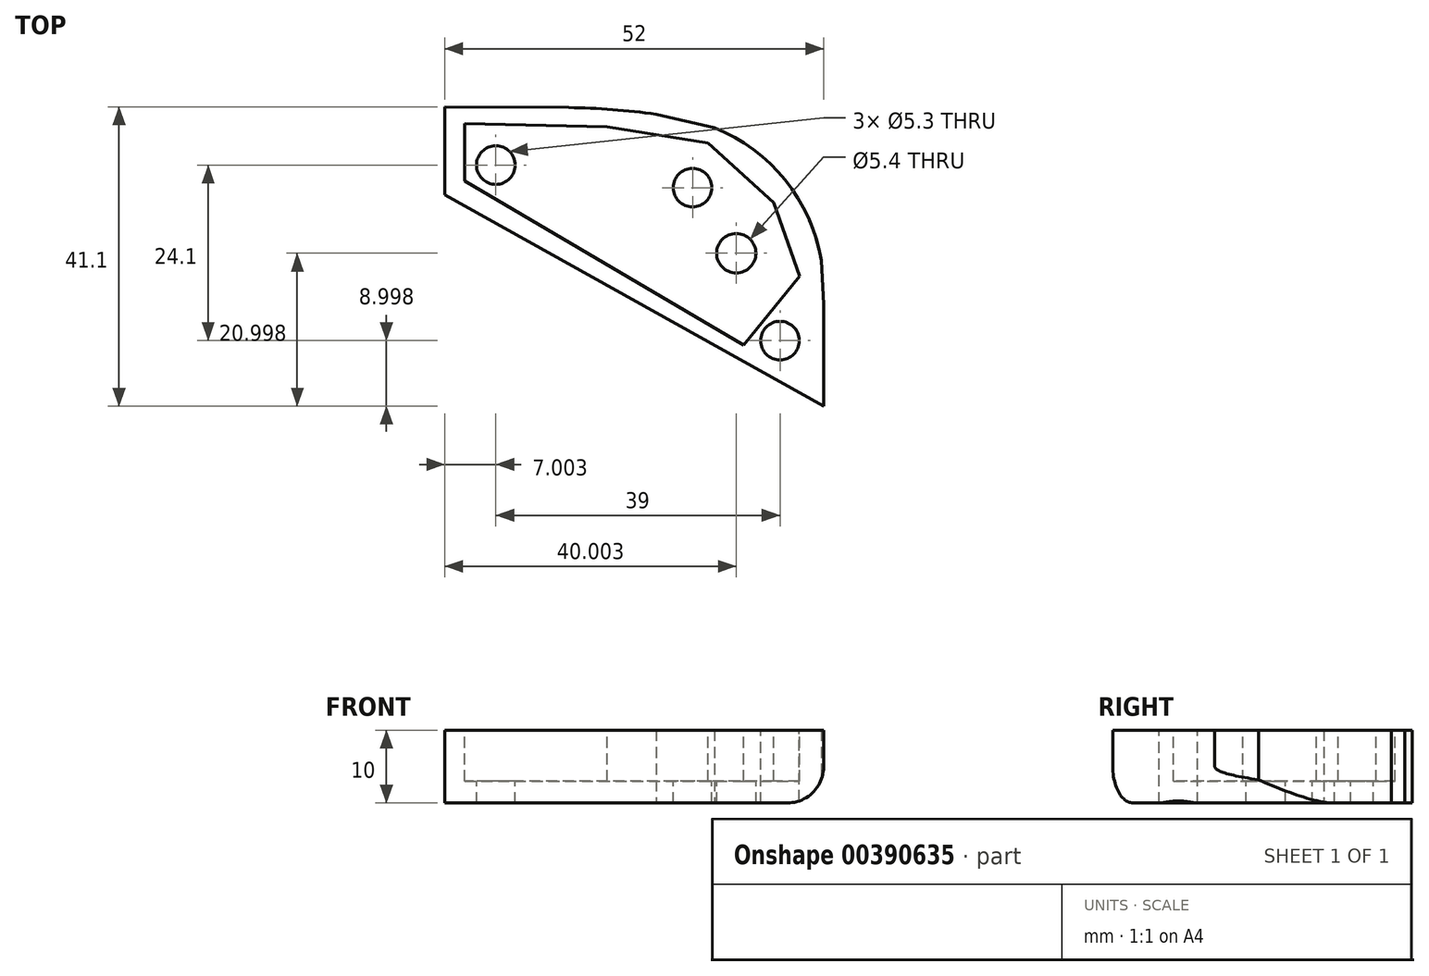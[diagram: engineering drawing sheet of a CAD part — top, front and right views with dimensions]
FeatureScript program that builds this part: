
annotation { "Feature Type Name" : "Feature", "Feature Type Description" : "" }
export const myFeature = defineFeature(function(context is Context, id is Id, definition is map)
    precondition{}
    {
        {
            var Q0;
            Q0=qCreatedBy(makeId("Top.planeOp"),FACE);
            var sketch = newSketch(context, id + "F0", { "sketchPlane" : qUnion([Q0])});
            skLineSegment(sketch, "E0", {"start": v(-50.84, -9.15) * mm, "end": v(-50.84, -21.25) * mm});
            skLineSegment(sketch, "E1", {"start": v(1.16, -50.25) * mm, "end": v(-50.84, -21.25) * mm});
            skLineSegment(sketch, "E2", {"start": v(1.16, -50.25) * mm, "end": v(1.16, -36.25) * mm});
            skArc(sketch, "E3", {"start": v(-13.84, -12) * mm, "mid": v(-4.13, -19.22) * mm, "end": v(0.83, -30.25) * mm});
            skLineSegment(sketch, "E4", {"start": v(-50.84, -9.15) * mm, "end": v(-33.84, -9.25) * mm});
            skArc(sketch, "E5", {"start": v(-33.84, -9.25) * mm, "mid": v(-27.82, -9.52) * mm, "end": v(-21.84, -10.15) * mm});
            skLineSegment(sketch, "E6", {"start": v(-21.84, -10.15) * mm, "end": v(-13.84, -12) * mm});
            skLineSegment(sketch, "E7", {"start": v(1.16, -36.25) * mm, "end": v(0.83, -30.25) * mm});
            skPoint(sketch, "E8.orphan", {"position": v(1.16, -34.25) * mm});
            skSolve(sketch);
        }
        {
            var Q0;
            Q0 = qSketchRegion(id + "F0", true);
            extrude(context, id + "F1", {"entities" : qUnion([Q0]), "depth" : 10 * mm});
        }
        {
            var Q0;
            Q0=makeQuery(id+"F1.opExtrude","CAP_FACE",FACE,{"disambiguationData":[OSD([sQuery(id+"F0.wireOp",EDGE,"sl27yMI0-AFCf-Kcrl-0bmQ-pZ9rT9zFnCGi"),sQuery(id+"F0.wireOp",EDGE,"BDBsffxZ-tEOx-Hil9-iUUA-GEFrlKPdEFfM"),sQuery(id+"F0.wireOp",EDGE,"E0"),sQuery(id+"F0.wireOp",EDGE,"E1"),sQuery(id+"F0.wireOp",EDGE,"E2"),sQuery(id+"F0.wireOp",EDGE,"E3"),sQuery(id+"F0.wireOp",EDGE,"15a26400-cb63-4f5f-8ce6-d631993ec03b")])],"isStart":false});
            var sketch = newSketch(context, id + "F2", { "sketchPlane" : qUnion([Q0])});
            skCircle(sketch, "E9", {"center": v(-43.84, -17.15) * mm, "radius": 2.65 * mm});
            skCircle(sketch, "E10", {"center": v(-16.84, -20.25) * mm, "radius": 2.65 * mm});
            skCircle(sketch, "E11", {"center": v(-4.84, -41.25) * mm, "radius": 2.65 * mm});
            skCircle(sketch, "E12", {"center": v(-10.84, -29.25) * mm, "radius": 2.7 * mm});
            skSolve(sketch);
        }
        {
            var Q0;
            Q0 = qSketchRegion(id + "F2", true);
            extrude(context, id + "F3", {"entities" : qUnion([Q0]), "operationType" : NewBodyOperationType.REMOVE, "endBound" : BoundingType.THROUGH_ALL, "oppositeDirection" : true, "depth" : 25 * mm});
        }
        {
            var Q0;
            Q0=makeQuery(id+"F1.opExtrude","CAP_EDGE",EDGE,{"disambiguationData":[OSD([sQuery(id+"F0.wireOp",EDGE,"E2")])],"isStart":true});
            fillet(context, id + "F4", {"entities" : qUnion([Q0]), "radius" : 5 * mm, "allowEdgeOverflow" : false});
        }
        {
            var Q0;
            Q0=makeQuery(id+"F2.imprint","IMPRINT",FACE,{"disambiguationData":[TD([[makeQuery(id+"F2.imprint","IMPRINT",EDGE,{"derivedFrom":sQuery(id+"F2.wireOp",EDGE,"E9")}),-1.0]])]});
            var sketch = newSketch(context, id + "F5", { "sketchPlane" : qUnion([Q0])});
            skLineSegment(sketch, "E13", {"start": v(-48.1, -11.48) * mm, "end": v(-48.1, -19.35) * mm});
            skLineSegment(sketch, "E14", {"start": v(-48.1, -19.35) * mm, "end": v(-9.82, -41.9) * mm});
            skLineSegment(sketch, "E15", {"start": v(-9.82, -41.9) * mm, "end": v(-2.17, -32.43) * mm});
            skLineSegment(sketch, "E16", {"start": v(-2.17, -32.43) * mm, "end": v(-5.68, -22.33) * mm});
            skLineSegment(sketch, "E17", {"start": v(-5.68, -22.33) * mm, "end": v(-14.71, -14.14) * mm});
            skLineSegment(sketch, "E18", {"start": v(-14.71, -14.14) * mm, "end": v(-28.54, -11.9) * mm});
            skLineSegment(sketch, "E19", {"start": v(-28.54, -11.9) * mm, "end": v(-48.1, -11.48) * mm});
            skSolve(sketch);
        }
        {
            var Q0;
            Q0 = qSketchRegion(id + "F5", true);
            extrude(context, id + "F6", {"entities" : qUnion([Q0]), "operationType" : NewBodyOperationType.REMOVE, "oppositeDirection" : true, "depth" : 7 * mm});
        }
    });
